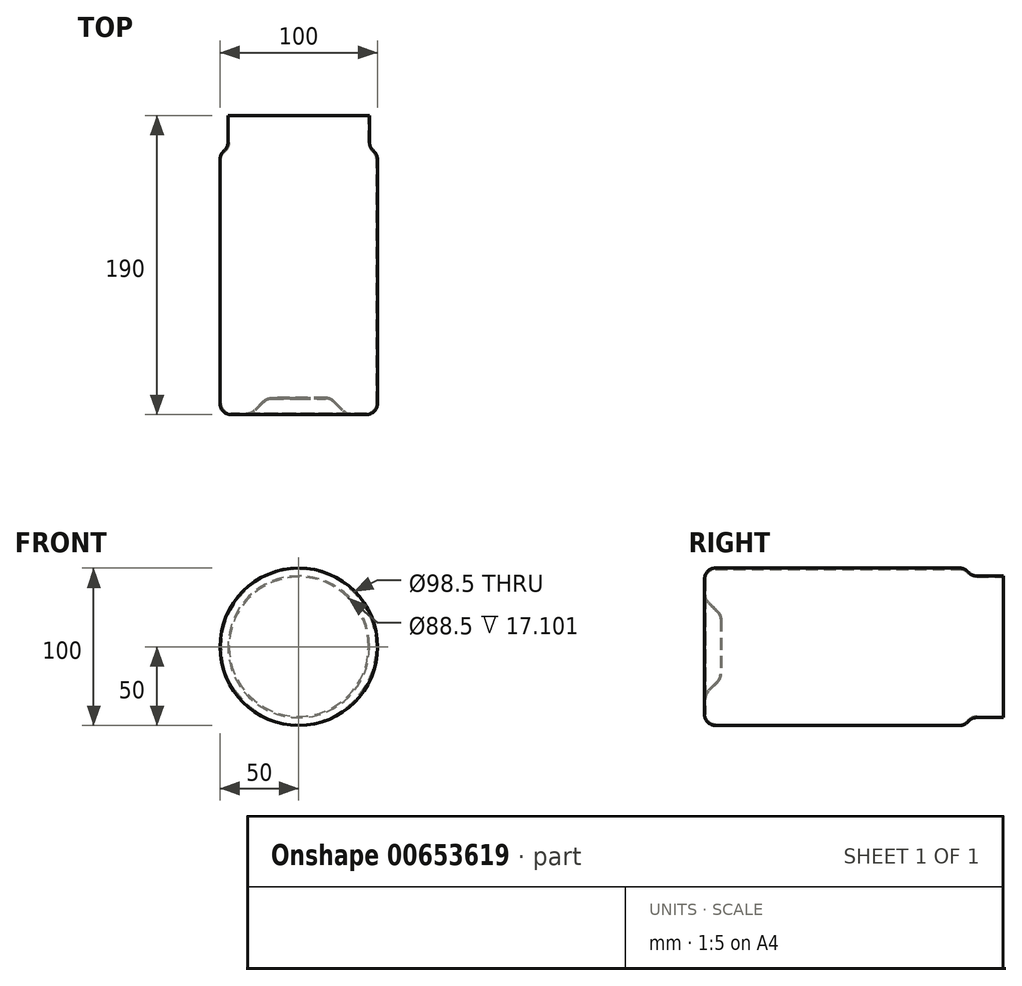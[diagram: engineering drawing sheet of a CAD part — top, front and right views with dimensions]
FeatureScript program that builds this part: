
annotation { "Feature Type Name" : "Feature", "Feature Type Description" : "" }
export const myFeature = defineFeature(function(context is Context, id is Id, definition is map)
    precondition{}
    {
        {
            var Q0;
            Q0=qCreatedBy(makeId("Top.planeOp"),FACE);
            var sketch = newSketch(context, id + "F0", { "sketchPlane" : qUnion([Q0])});
            skLineSegment(sketch, "E0", {"start": v(0, 105) * mm, "end": v(0, -105) * mm});
            skLineSegment(sketch, "E1", {"start": v(-70, 0) * mm, "end": v(70, 0) * mm});
            skLineSegment(sketch, "E2", {"start": v(-32.9, -95) * mm, "end": v(-43, -95) * mm});
            skLineSegment(sketch, "E3", {"start": v(-50, -88) * mm, "end": v(-50, 67.1) * mm});
            skLineSegment(sketch, "E4", {"start": v(-47.05, 72.95) * mm, "end": v(-47.95, 72.05) * mm});
            skLineSegment(sketch, "E5", {"start": v(-45, 95) * mm, "end": v(-45, 77.9) * mm});
            skArc(sketch, "E6", {"start": v(-47.95, 72.05) * mm, "mid": v(-49.47, 69.78) * mm, "end": v(-50, 67.1) * mm});
            skArc(sketch, "E7", {"start": v(-47.05, 72.95) * mm, "mid": v(-45.53, 75.22) * mm, "end": v(-45, 77.9) * mm});
            skArc(sketch, "E8", {"start": v(-50, -88) * mm, "mid": v(-47.95, -92.95) * mm, "end": v(-43, -95) * mm});
            skLineSegment(sketch, "E9", {"start": v(-44.25, 95) * mm, "end": v(-44.25, 77.9) * mm});
            skArc(sketch, "E10", {"start": v(-46.52, 72.42) * mm, "mid": v(-44.84, 74.93) * mm, "end": v(-44.25, 77.9) * mm});
            skArc(sketch, "E11", {"start": v(-47.42, 71.52) * mm, "mid": v(-48.77, 69.5) * mm, "end": v(-49.25, 67.1) * mm});
            skLineSegment(sketch, "E12", {"start": v(-49.25, -88) * mm, "end": v(-49.25, 67.1) * mm});
            skLineSegment(sketch, "E13", {"start": v(-46.52, 72.42) * mm, "end": v(-47.42, 71.52) * mm});
            skArc(sketch, "E14", {"start": v(-49.25, -88) * mm, "mid": v(-47.42, -92.42) * mm, "end": v(-43, -94.25) * mm});
            skLineSegment(sketch, "E15", {"start": v(-45, 95) * mm, "end": v(-44.25, 95) * mm});
            skLineSegment(sketch, "E16", {"start": v(0, -85) * mm, "end": v(-17.1, -85) * mm});
            skLineSegment(sketch, "E17", {"start": v(-27.95, -92.95) * mm, "end": v(-22.05, -87.05) * mm});
            skArc(sketch, "E18", {"start": v(-17.1, -85) * mm, "mid": v(-19.78, -85.53) * mm, "end": v(-22.05, -87.05) * mm});
            skArc(sketch, "E19", {"start": v(-32.9, -95) * mm, "mid": v(-30.22, -94.47) * mm, "end": v(-27.95, -92.95) * mm});
            skLineSegment(sketch, "E20", {"start": v(-32.9, -94.25) * mm, "end": v(-43, -94.25) * mm});
            skArc(sketch, "E21", {"start": v(-32.9, -94.25) * mm, "mid": v(-30.5, -93.77) * mm, "end": v(-28.48, -92.42) * mm});
            skLineSegment(sketch, "E22", {"start": v(-28.48, -92.42) * mm, "end": v(-22.58, -86.52) * mm});
            skArc(sketch, "E23", {"start": v(-17.1, -84.25) * mm, "mid": v(-20.07, -84.84) * mm, "end": v(-22.58, -86.52) * mm});
            skLineSegment(sketch, "E24", {"start": v(0, -84.25) * mm, "end": v(-17.1, -84.25) * mm});
            skLineSegment(sketch, "E25", {"start": v(0, -84.25) * mm, "end": v(0, -85) * mm});
            skSolve(sketch);
        }
        {
            var Q0;
            Q0=makeQuery(id+"F0.imprint","IMPRINT",FACE,{"disambiguationData":[TD([[makeQuery(id+"F0.imprint","IMPRINT",EDGE,{"derivedFrom":sQuery(id+"F0.wireOp",EDGE,"E4")}),1.0]])]});
            var Q1;
            Q1=makeQuery(id+"F0.imprint","IMPRINT",FACE,{"disambiguationData":[TD([[makeQuery(id+"F0.imprint","IMPRINT",EDGE,{"derivedFrom":sQuery(id+"F0.wireOp",EDGE,"E2")}),-1.0]])]});
            var Q2;
            Q2=sQuery(id+"F0.wireOp",EDGE,"E0");
            revolve(context, id + "F1", {"entities" : qUnion([Q0, Q1]), "axis" : qUnion([Q2]), "revolveType" : RevolveType.FULL});
        }
    });
